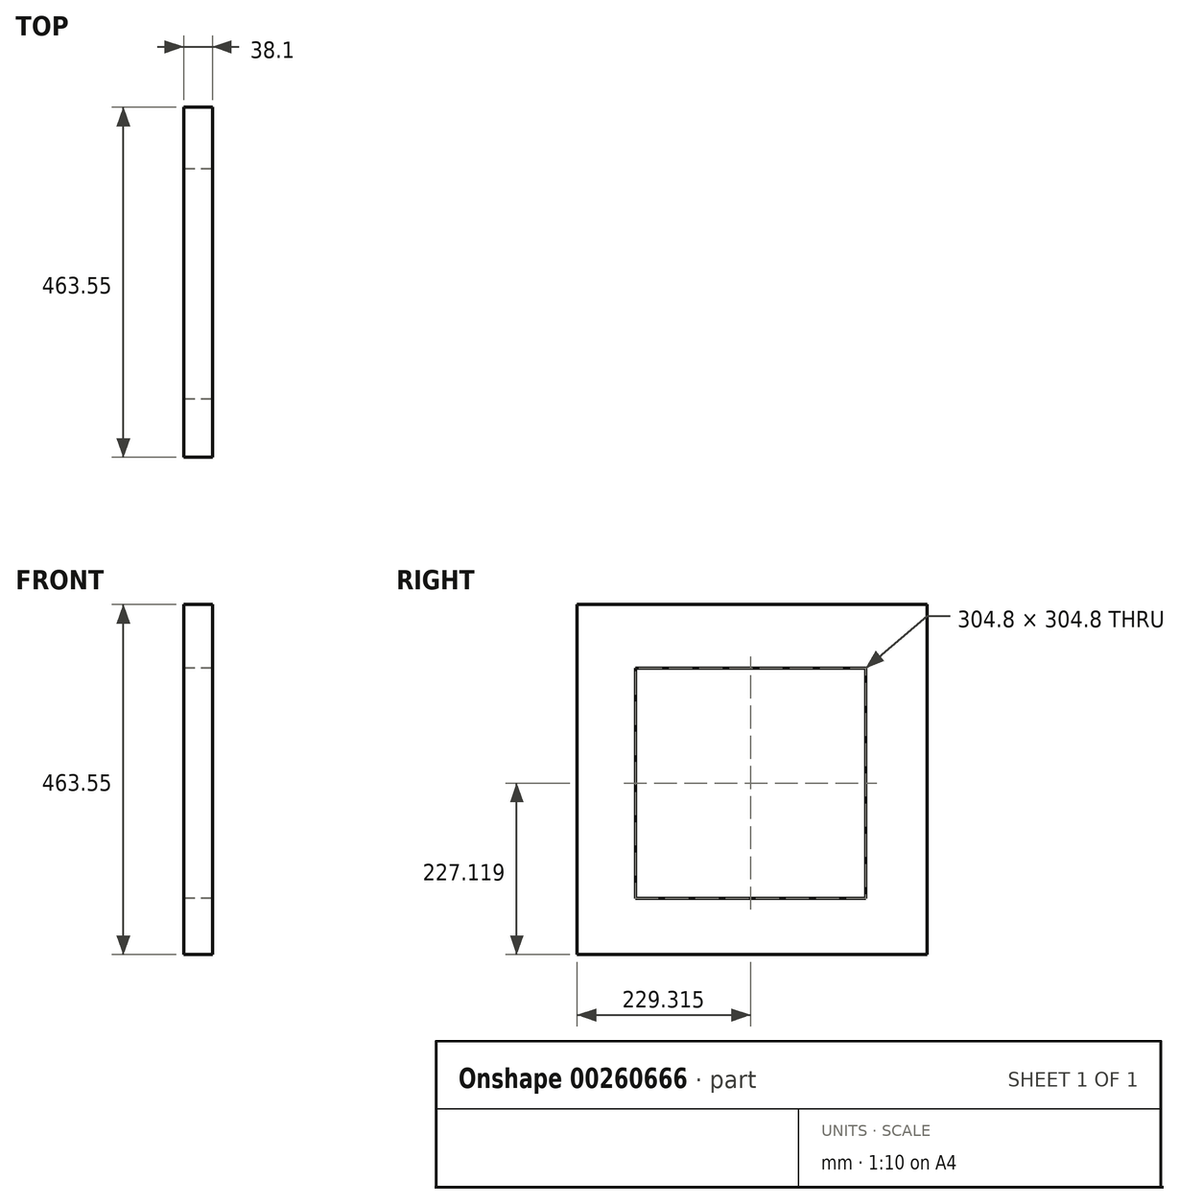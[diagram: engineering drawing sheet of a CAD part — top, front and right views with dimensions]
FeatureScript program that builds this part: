
annotation { "Feature Type Name" : "Feature", "Feature Type Description" : "" }
export const myFeature = defineFeature(function(context is Context, id is Id, definition is map)
    precondition{}
    {
        {
            var Q0;
            Q0=qCreatedBy(makeId("Right.planeOp"),FACE);
            var sketch = newSketch(context, id + "F0", { "sketchPlane" : qUnion([Q0])});
            skLineSegment(sketch, "E0.bottom", {"start": v(-242.95, 240.57) * mm, "end": v(220.6, 240.57) * mm});
            skLineSegment(sketch, "E0.top", {"start": v(-242.95, -222.98) * mm, "end": v(220.6, -222.98) * mm});
            skLineSegment(sketch, "E0.left", {"start": v(-242.95, 240.57) * mm, "end": v(-242.95, -222.98) * mm});
            skLineSegment(sketch, "E0.right", {"start": v(220.6, 240.57) * mm, "end": v(220.6, -222.98) * mm});
            skLineSegment(sketch, "E1.bottom", {"start": v(-166.03, 156.54) * mm, "end": v(138.77, 156.54) * mm});
            skLineSegment(sketch, "E1.top", {"start": v(-166.03, -148.26) * mm, "end": v(138.77, -148.26) * mm});
            skLineSegment(sketch, "E1.left", {"start": v(-166.03, 156.54) * mm, "end": v(-166.03, -148.26) * mm});
            skLineSegment(sketch, "E1.right", {"start": v(138.77, 156.54) * mm, "end": v(138.77, -148.26) * mm});
            skSolve(sketch);
        }
        {
            var Q0;
            Q0 = qSketchRegion(id + "F0", true);
            extrude(context, id + "F1", {"entities" : qUnion([Q0]), "depth" : 38.1 * mm});
        }
    });
